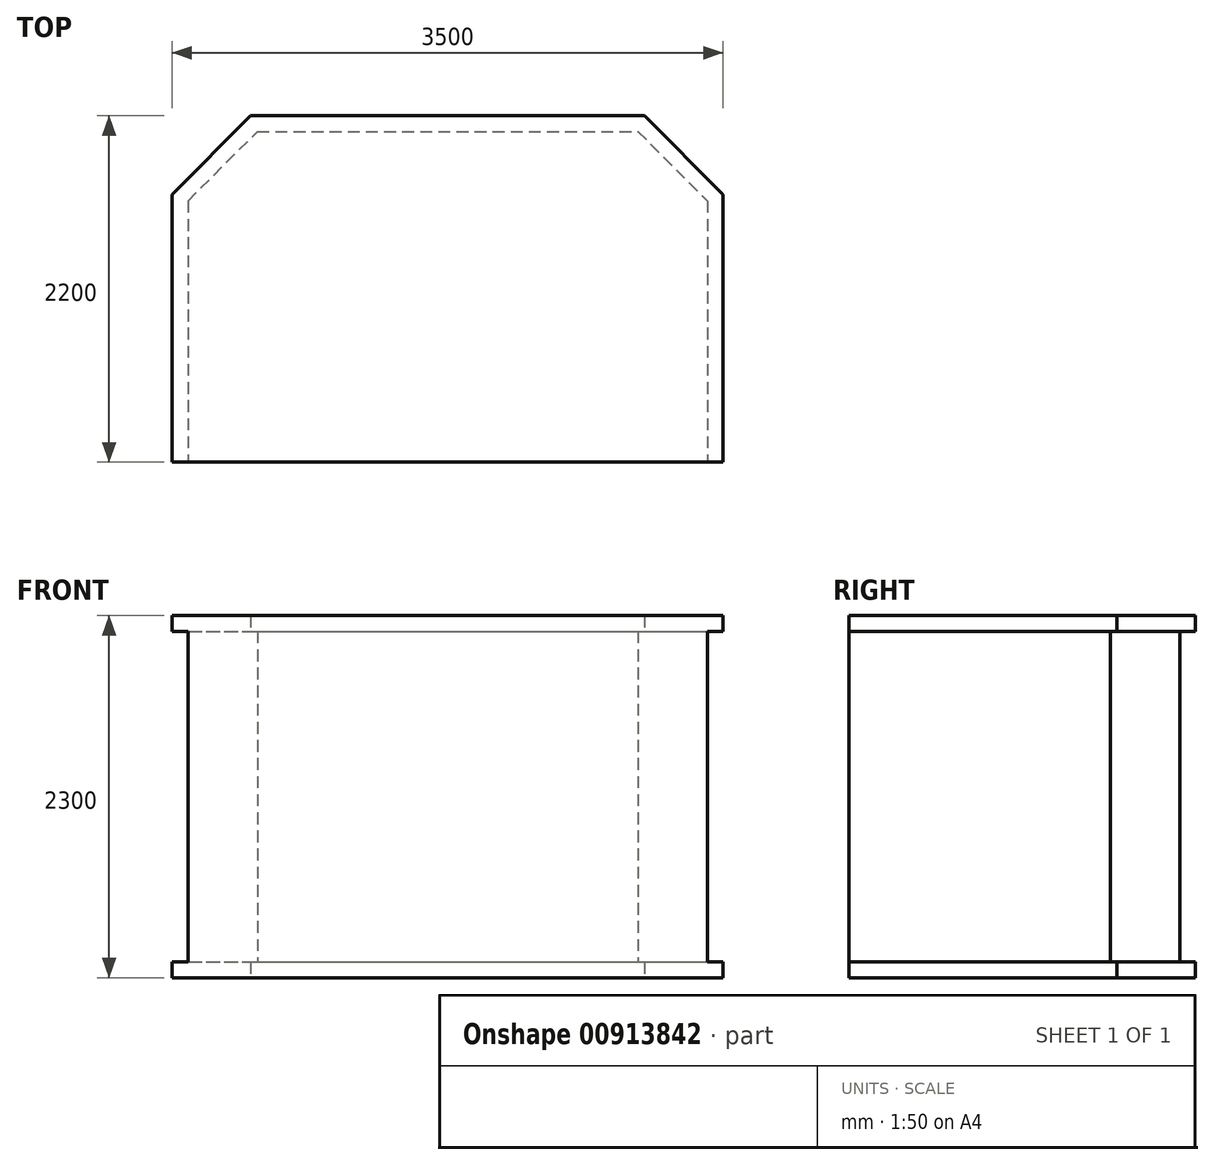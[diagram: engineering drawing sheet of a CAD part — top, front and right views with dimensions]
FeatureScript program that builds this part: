
annotation { "Feature Type Name" : "Feature", "Feature Type Description" : "" }
export const myFeature = defineFeature(function(context is Context, id is Id, definition is map)
    precondition{}
    {
        {
            var Q0;
            Q0=qCreatedBy(makeId("Top.planeOp"),FACE);
            var sketch = newSketch(context, id + "F0", { "sketchPlane" : qUnion([Q0])});
            skLineSegment(sketch, "E0.bottom", {"start": v(1250, 1100) * mm, "end": v(-1250, 1100) * mm});
            skLineSegment(sketch, "E0.top", {"start": v(1750, -1100) * mm, "end": v(-1750, -1100) * mm});
            skLineSegment(sketch, "E0.left", {"start": v(1750, 600) * mm, "end": v(1750, -1100) * mm});
            skLineSegment(sketch, "E0.right", {"start": v(-1750, 600) * mm, "end": v(-1750, -1100) * mm});
            skPoint(sketch, "E0.middle", {"position": v(0, 0) * mm});
            skLineSegment(sketch, "E1", {"start": v(1250, 1100) * mm, "end": v(1750, 600) * mm});
            skLineSegment(sketch, "E2", {"start": v(-1750, 600) * mm, "end": v(-1250, 1100) * mm});
            skPoint(sketch, "E3.orphan", {"position": v(-1750, 1100) * mm});
            skPoint(sketch, "E4.orphan", {"position": v(1750, 1100) * mm});
            skSolve(sketch);
        }
        {
            var Q0;
            Q0 = qSketchRegion(id + "F0", true);
            extrude(context, id + "F1", {"entities" : qUnion([Q0]), "depth" : 2300 * mm, "offsetDistance" : 25 * mm});
        }
        {
            var Q0;
            Q0=makeQuery(id+"F1.opExtrude","SWEPT_FACE",FACE,{"disambiguationData":[OSD([sQuery(id+"F0.wireOp",EDGE,"E0.right")])]});
            var sketch = newSketch(context, id + "F2", { "sketchPlane" : qUnion([Q0])});
            skLineSegment(sketch, "E5.bottom", {"start": v(-600, 2200) * mm, "end": v(1100, 2200) * mm});
            skLineSegment(sketch, "E5.top", {"start": v(-600, 100) * mm, "end": v(1100, 100) * mm});
            skLineSegment(sketch, "E5.left", {"start": v(-600, 2200) * mm, "end": v(-600, 100) * mm});
            skLineSegment(sketch, "E5.right", {"start": v(1100, 2200) * mm, "end": v(1100, 100) * mm});
            skSolve(sketch);
        }
        {
            var Q0;
            Q0 = qSketchRegion(id + "F2", true);
            extrude(context, id + "F3", {"entities" : qUnion([Q0]), "operationType" : NewBodyOperationType.REMOVE, "oppositeDirection" : true, "depth" : 100 * mm, "offsetDistance" : 25 * mm});
        }
        {
            var Q0;
            Q0=makeQuery(id+"F1.opExtrude","SWEPT_FACE",FACE,{"disambiguationData":[OSD([sQuery(id+"F0.wireOp",EDGE,"E2")])]});
            var sketch = newSketch(context, id + "F4", { "sketchPlane" : qUnion([Q0])});
            skLineSegment(sketch, "E6.bottom", {"start": v(813.17, 2200) * mm, "end": v(106.07, 2200) * mm});
            skLineSegment(sketch, "E6.top", {"start": v(813.17, 100) * mm, "end": v(106.07, 100) * mm});
            skLineSegment(sketch, "E6.left", {"start": v(813.17, 2200) * mm, "end": v(813.17, 100) * mm});
            skLineSegment(sketch, "E6.right", {"start": v(106.07, 2200) * mm, "end": v(106.07, 100) * mm});
            skSolve(sketch);
        }
        {
            var Q0;
            Q0 = qSketchRegion(id + "F4", true);
            extrude(context, id + "F5", {"entities" : qUnion([Q0]), "operationType" : NewBodyOperationType.REMOVE, "oppositeDirection" : true, "depth" : 100 * mm, "offsetDistance" : 25 * mm});
        }
        {
            var Q0;
            Q0=makeQuery(id+"F1.opExtrude","SWEPT_FACE",FACE,{"disambiguationData":[OSD([sQuery(id+"F0.wireOp",EDGE,"E0.bottom")])]});
            var sketch = newSketch(context, id + "F6", { "sketchPlane" : qUnion([Q0])});
            skLineSegment(sketch, "E7.bottom", {"start": v(1250, 2200) * mm, "end": v(-1250, 2200) * mm});
            skLineSegment(sketch, "E7.top", {"start": v(1250, 100) * mm, "end": v(-1250, 100) * mm});
            skLineSegment(sketch, "E7.left", {"start": v(1250, 2200) * mm, "end": v(1250, 100) * mm});
            skLineSegment(sketch, "E7.right", {"start": v(-1250, 2200) * mm, "end": v(-1250, 100) * mm});
            skSolve(sketch);
        }
        {
            var Q0;
            Q0 = qSketchRegion(id + "F6", true);
            extrude(context, id + "F7", {"entities" : qUnion([Q0]), "operationType" : NewBodyOperationType.REMOVE, "oppositeDirection" : true, "depth" : 100 * mm, "offsetDistance" : 25 * mm});
        }
        {
            var Q0;
            Q0=makeQuery(id+"F1.opExtrude","SWEPT_FACE",FACE,{"disambiguationData":[OSD([sQuery(id+"F0.wireOp",EDGE,"E1")])]});
            var sketch = newSketch(context, id + "F8", { "sketchPlane" : qUnion([Q0])});
            skLineSegment(sketch, "E8.bottom", {"start": v(-106.07, 2200) * mm, "end": v(-813.17, 2200) * mm});
            skLineSegment(sketch, "E8.top", {"start": v(-106.07, 100) * mm, "end": v(-813.17, 100) * mm});
            skLineSegment(sketch, "E8.left", {"start": v(-106.07, 2200) * mm, "end": v(-106.07, 100) * mm});
            skLineSegment(sketch, "E8.right", {"start": v(-813.17, 2200) * mm, "end": v(-813.17, 100) * mm});
            skSolve(sketch);
        }
        {
            var Q0;
            Q0 = qSketchRegion(id + "F8", true);
            extrude(context, id + "F9", {"entities" : qUnion([Q0]), "operationType" : NewBodyOperationType.REMOVE, "oppositeDirection" : true, "depth" : 100 * mm, "offsetDistance" : 25 * mm});
        }
        {
            var Q0;
            Q0=makeQuery(id+"F1.opExtrude","SWEPT_FACE",FACE,{"disambiguationData":[OSD([sQuery(id+"F0.wireOp",EDGE,"E0.left")])]});
            var sketch = newSketch(context, id + "F10", { "sketchPlane" : qUnion([Q0])});
            skLineSegment(sketch, "E9.bottom", {"start": v(600, 2200) * mm, "end": v(-1100, 2200) * mm});
            skLineSegment(sketch, "E9.top", {"start": v(600, 100) * mm, "end": v(-1100, 100) * mm});
            skLineSegment(sketch, "E9.left", {"start": v(600, 2200) * mm, "end": v(600, 100) * mm});
            skLineSegment(sketch, "E9.right", {"start": v(-1100, 2200) * mm, "end": v(-1100, 100) * mm});
            skSolve(sketch);
        }
        {
            var Q0;
            Q0 = qSketchRegion(id + "F10", true);
            extrude(context, id + "F11", {"entities" : qUnion([Q0]), "operationType" : NewBodyOperationType.REMOVE, "oppositeDirection" : true, "depth" : 100 * mm, "offsetDistance" : 25 * mm});
        }
    });
